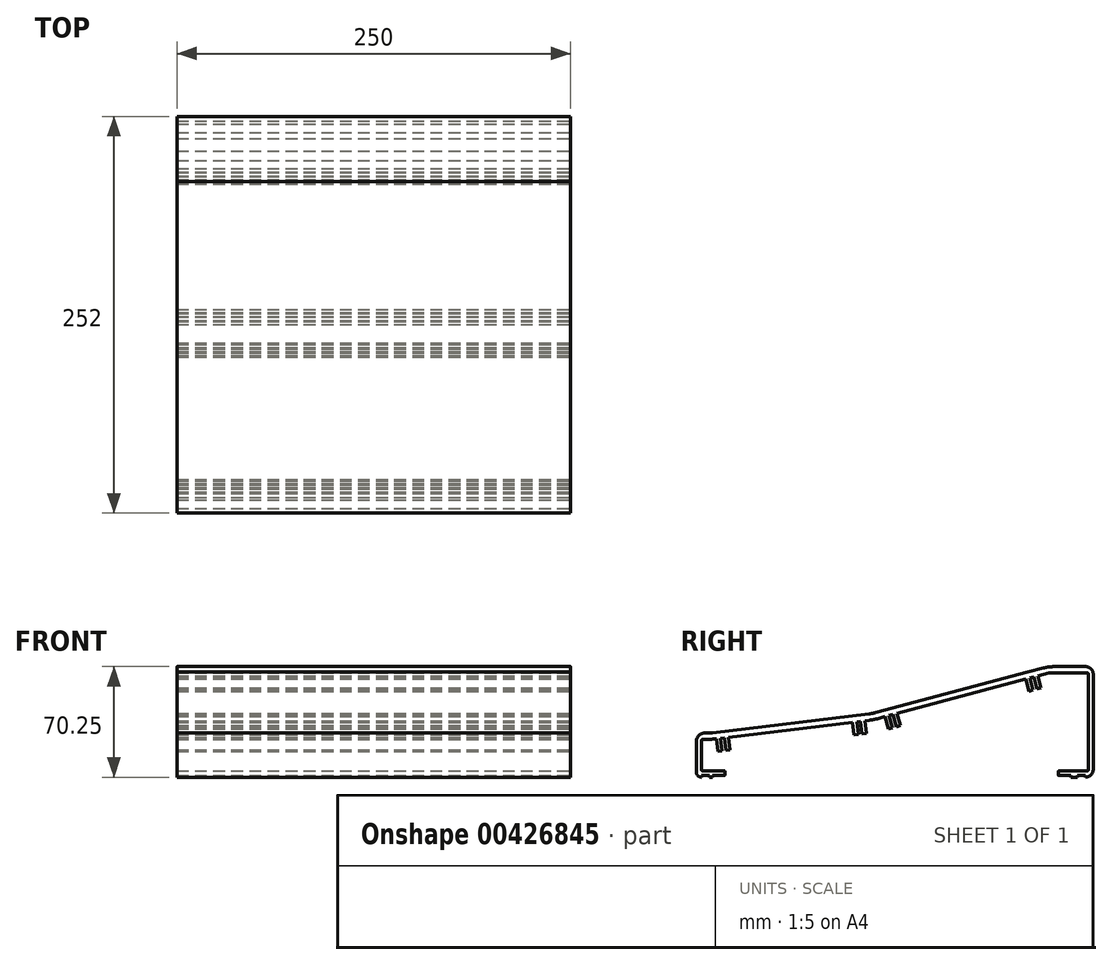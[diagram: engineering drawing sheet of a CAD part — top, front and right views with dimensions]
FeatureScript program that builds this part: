
annotation { "Feature Type Name" : "Feature", "Feature Type Description" : "" }
export const myFeature = defineFeature(function(context is Context, id is Id, definition is map)
    precondition{}
    {
        {
            var Q0;
            Q0=qCreatedBy(makeId("Right.planeOp"),FACE);
            var sketch = newSketch(context, id + "F0", { "sketchPlane" : qUnion([Q0])});
            skLineSegment(sketch, "E0", {"start": v(-67.21, 3) * mm, "end": v(-67.21, 23) * mm});
            skLineSegment(sketch, "E1", {"start": v(-62.21, 28) * mm, "end": v(-60.21, 28) * mm});
            skLineSegment(sketch, "E2", {"start": v(-57.1, 28.19) * mm, "end": v(42.18, 40.15) * mm});
            skLineSegment(sketch, "E3", {"start": v(46.7, 41.02) * mm, "end": v(143.32, 66.82) * mm});
            skPoint(sketch, "E4.visualSharp", {"position": v(-67.21, 28) * mm});
            skArc(sketch, "E4.filletArc", {"start": v(-62.21, 28) * mm, "mid": v(-65.75, 26.54) * mm, "end": v(-67.21, 23) * mm});
            skPoint(sketch, "E5.visualSharp", {"position": v(184.79, 70.25) * mm});
            skPoint(sketch, "E6.visualSharp", {"position": v(150.58, 68.76) * mm});
            skPoint(sketch, "E7.visualSharp", {"position": v(44.47, 40.43) * mm});
            skArc(sketch, "E7.filletArc", {"start": v(42.18, 40.15) * mm, "mid": v(44.46, 40.5) * mm, "end": v(46.7, 41.02) * mm});
            skPoint(sketch, "E8.visualSharp", {"position": v(-58.65, 28) * mm});
            skArc(sketch, "E8.filletArc", {"start": v(-60.21, 28) * mm, "mid": v(-58.65, 28.05) * mm, "end": v(-57.1, 28.19) * mm});
            skLineSegment(sketch, "E9.1", {"start": v(156.59, 66.23) * mm, "end": v(180.79, 66.25) * mm});
            skLineSegment(sketch, "E9.3", {"start": v(47.73, 37.16) * mm, "end": v(156.59, 66.23) * mm});
            skArc(sketch, "E9.4", {"start": v(42.66, 36.18) * mm, "mid": v(45.21, 36.58) * mm, "end": v(47.73, 37.16) * mm});
            skLineSegment(sketch, "E9.6", {"start": v(-63.21, 24) * mm, "end": v(-60.21, 24) * mm});
            skArc(sketch, "E9.7", {"start": v(-60.21, 24) * mm, "mid": v(-58.41, 24.05) * mm, "end": v(-56.62, 24.22) * mm});
            skLineSegment(sketch, "E9.8", {"start": v(-56.62, 24.22) * mm, "end": v(42.66, 36.18) * mm});
            skLineSegment(sketch, "E10", {"start": v(-59.01, 0) * mm, "end": v(-57.2, 0) * mm});
            skPoint(sketch, "E11.visualSharp", {"position": v(-67.21, 0) * mm});
            skArc(sketch, "E11.filletArc", {"start": v(-67.21, 3) * mm, "mid": v(-66.33, 0.88) * mm, "end": v(-64.21, 0) * mm});
            skLineSegment(sketch, "E12", {"start": v(170.59, 0) * mm, "end": v(174.59, 0) * mm});
            skPoint(sketch, "E13.visualSharp", {"position": v(181.57, 0) * mm});
            skLineSegment(sketch, "E14.0", {"start": v(-64.21, 5) * mm, "end": v(-64.21, 23) * mm});
            skLineSegment(sketch, "E15", {"start": v(160.42, 70.23) * mm, "end": v(179.78, 70.25) * mm});
            skLineSegment(sketch, "E16", {"start": v(184.79, 65.25) * mm, "end": v(184.79, 5) * mm});
            skArc(sketch, "E17.filletArc", {"start": v(184.79, 65.25) * mm, "mid": v(183.32, 68.78) * mm, "end": v(179.78, 70.25) * mm});
            skLineSegment(sketch, "E18", {"start": v(181.79, 5) * mm, "end": v(181.79, 65.25) * mm});
            skPoint(sketch, "E19.visualSharp", {"position": v(181.79, 66.25) * mm});
            skArc(sketch, "E19.filletArc", {"start": v(181.79, 65.25) * mm, "mid": v(181.5, 65.95) * mm, "end": v(180.79, 66.25) * mm});
            skArc(sketch, "E20.filletArc", {"start": v(-63.21, 24) * mm, "mid": v(-63.92, 23.7) * mm, "end": v(-64.21, 23) * mm});
            skLineSegment(sketch, "E21", {"start": v(-64.21, 0) * mm, "end": v(-64.21, 1) * mm});
            skLineSegment(sketch, "E22", {"start": v(-64.21, 1) * mm, "end": v(-59.01, 1) * mm});
            skLineSegment(sketch, "E23", {"start": v(-59.01, 1) * mm, "end": v(-59.01, 0) * mm});
            skLineSegment(sketch, "E24", {"start": v(179.79, 0) * mm, "end": v(179.79, 1) * mm});
            skLineSegment(sketch, "E25", {"start": v(179.79, 1) * mm, "end": v(174.59, 1) * mm});
            skLineSegment(sketch, "E26", {"start": v(174.59, 1) * mm, "end": v(174.59, 0) * mm});
            skPoint(sketch, "E27.visualSharp", {"position": v(184.79, 0) * mm});
            skArc(sketch, "E27.filletArc", {"start": v(179.79, 0) * mm, "mid": v(183.32, 1.46) * mm, "end": v(184.79, 5) * mm});
            skLineSegment(sketch, "E28", {"start": v(-57.2, 0) * mm, "end": v(-57.2, 1) * mm});
            skLineSegment(sketch, "E29", {"start": v(-57.2, 1) * mm, "end": v(-49.4, 1) * mm});
            skLineSegment(sketch, "E30", {"start": v(-49.2, 1.2) * mm, "end": v(-49.2, 3.8) * mm});
            skLineSegment(sketch, "E31", {"start": v(-49.4, 4) * mm, "end": v(-63.21, 4) * mm});
            skArc(sketch, "E32.filletArc", {"start": v(-64.21, 5) * mm, "mid": v(-63.92, 4.3) * mm, "end": v(-63.21, 4) * mm});
            skPoint(sketch, "E33.visualSharp", {"position": v(-49.2, 4) * mm});
            skArc(sketch, "E33.filletArc", {"start": v(-49.2, 3.8) * mm, "mid": v(-49.25, 3.94) * mm, "end": v(-49.4, 4) * mm});
            skPoint(sketch, "E34.visualSharp", {"position": v(-49.2, 1) * mm});
            skArc(sketch, "E34.filletArc", {"start": v(-49.4, 1) * mm, "mid": v(-49.25, 1.06) * mm, "end": v(-49.2, 1.2) * mm});
            skLineSegment(sketch, "E35", {"start": v(170.59, 0) * mm, "end": v(170.59, 1) * mm});
            skLineSegment(sketch, "E36", {"start": v(170.59, 1) * mm, "end": v(162.79, 1) * mm});
            skLineSegment(sketch, "E37", {"start": v(162.59, 1.2) * mm, "end": v(162.59, 3.8) * mm});
            skLineSegment(sketch, "E38", {"start": v(162.79, 4) * mm, "end": v(180.79, 4) * mm});
            skArc(sketch, "E39.filletArc", {"start": v(180.79, 4) * mm, "mid": v(181.5, 4.3) * mm, "end": v(181.79, 5) * mm});
            skPoint(sketch, "E40.visualSharp", {"position": v(162.59, 4) * mm});
            skArc(sketch, "E40.filletArc", {"start": v(162.79, 4) * mm, "mid": v(162.65, 3.94) * mm, "end": v(162.59, 3.8) * mm});
            skPoint(sketch, "E41.visualSharp", {"position": v(162.59, 1) * mm});
            skArc(sketch, "E41.filletArc", {"start": v(162.59, 1.2) * mm, "mid": v(162.65, 1.06) * mm, "end": v(162.79, 1) * mm});
            skPoint(sketch, "E42.orphan", {"position": v(-50.17, 0) * mm});
            skLineSegment(sketch, "E43", {"start": v(-54.62, 24.46) * mm, "end": v(-53.66, 16.51) * mm});
            skLineSegment(sketch, "E44", {"start": v(-53.66, 16.51) * mm, "end": v(-50.98, 16.84) * mm});
            skLineSegment(sketch, "E45", {"start": v(-50.98, 16.84) * mm, "end": v(-51.94, 24.78) * mm});
            skLineSegment(sketch, "E46", {"start": v(-49.46, 25.08) * mm, "end": v(-48.5, 17.14) * mm});
            skLineSegment(sketch, "E47", {"start": v(-48.5, 17.14) * mm, "end": v(-45.82, 17.46) * mm});
            skLineSegment(sketch, "E48", {"start": v(-45.82, 17.46) * mm, "end": v(-46.78, 25.4) * mm});
            skLineSegment(sketch, "E49", {"start": v(153.03, 69.3) * mm, "end": v(143.32, 66.82) * mm});
            skPoint(sketch, "E50.visualSharp", {"position": v(156.66, 70.23) * mm});
            skArc(sketch, "E50.filletArc", {"start": v(160.42, 70.23) * mm, "mid": v(156.7, 70) * mm, "end": v(153.03, 69.3) * mm});
            skLineSegment(sketch, "E51", {"start": v(31.87, 34.88) * mm, "end": v(32.83, 26.94) * mm});
            skLineSegment(sketch, "E52", {"start": v(32.83, 26.94) * mm, "end": v(35.5, 27.26) * mm});
            skLineSegment(sketch, "E53", {"start": v(35.5, 27.26) * mm, "end": v(34.55, 35.2) * mm});
            skLineSegment(sketch, "E54", {"start": v(37.03, 35.5) * mm, "end": v(37.99, 27.56) * mm});
            skLineSegment(sketch, "E55", {"start": v(37.99, 27.56) * mm, "end": v(40.67, 27.88) * mm});
            skLineSegment(sketch, "E56", {"start": v(40.67, 27.88) * mm, "end": v(39.71, 35.83) * mm});
            skLineSegment(sketch, "E57", {"start": v(52.53, 38.44) * mm, "end": v(54.6, 30.71) * mm});
            skLineSegment(sketch, "E58", {"start": v(54.6, 30.71) * mm, "end": v(57.2, 31.4) * mm});
            skLineSegment(sketch, "E59", {"start": v(57.2, 31.4) * mm, "end": v(55.14, 39.14) * mm});
            skLineSegment(sketch, "E60", {"start": v(57.56, 39.78) * mm, "end": v(59.62, 32.05) * mm});
            skLineSegment(sketch, "E61", {"start": v(59.62, 32.05) * mm, "end": v(62.23, 32.75) * mm});
            skLineSegment(sketch, "E62", {"start": v(62.23, 32.75) * mm, "end": v(60.16, 40.48) * mm});
            skLineSegment(sketch, "E63", {"start": v(149.55, 64.35) * mm, "end": v(151.61, 56.62) * mm});
            skLineSegment(sketch, "E64", {"start": v(151.61, 56.62) * mm, "end": v(149, 55.92) * mm});
            skLineSegment(sketch, "E65", {"start": v(149, 55.92) * mm, "end": v(146.94, 63.65) * mm});
            skLineSegment(sketch, "E66", {"start": v(144.53, 63) * mm, "end": v(146.59, 55.28) * mm});
            skLineSegment(sketch, "E67", {"start": v(146.59, 55.28) * mm, "end": v(143.98, 54.58) * mm});
            skLineSegment(sketch, "E68", {"start": v(143.98, 54.58) * mm, "end": v(141.92, 62.3) * mm});
            skSolve(sketch);
        }
        {
            var Q0;
            Q0=qSketchRegion(id+"F0",true);
            extrude(context, id + "F1", {"entities" : qUnion([Q0]), "oppositeDirection" : true, "depth" : 250 * mm});
        }
    });
